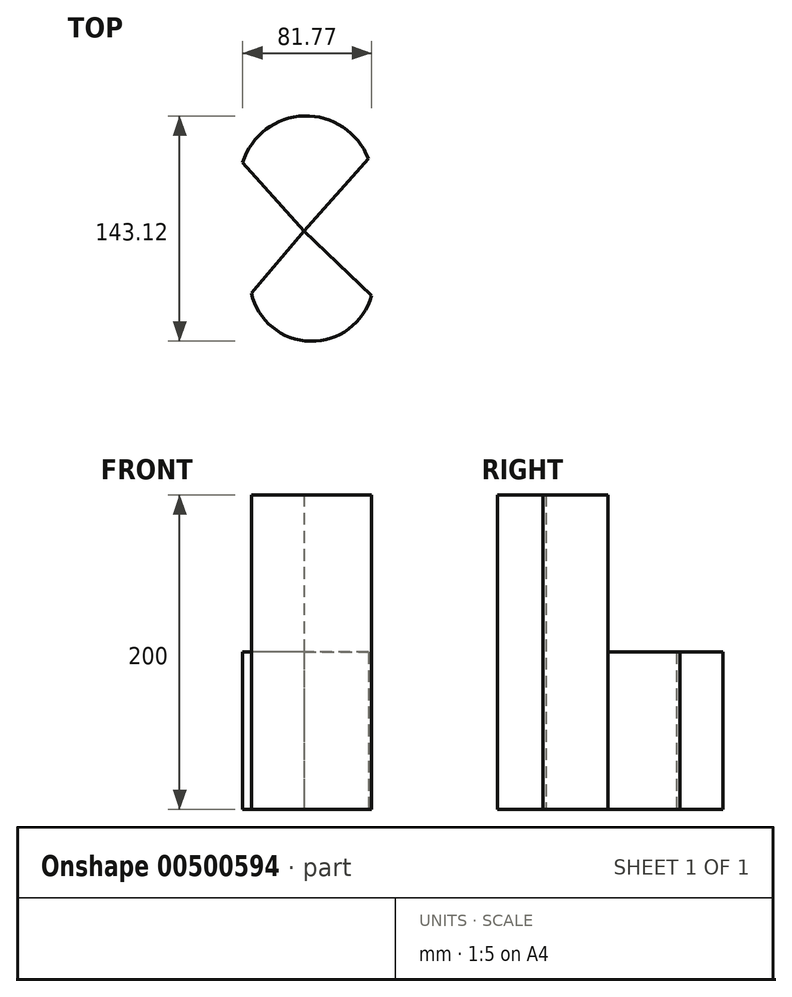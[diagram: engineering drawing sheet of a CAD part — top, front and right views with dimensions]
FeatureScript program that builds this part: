
annotation { "Feature Type Name" : "Feature", "Feature Type Description" : "" }
export const myFeature = defineFeature(function(context is Context, id is Id, definition is map)
    precondition{}
    {
        {
            var Q0;
            Q0=qCreatedBy(makeId("Top.planeOp"),FACE);
            var sketch = newSketch(context, id + "F0", { "sketchPlane" : qUnion([Q0])});
            skLineSegment(sketch, "E0", {"start": v(0, 0) * mm, "end": v(40.74, 45.76) * mm});
            skLineSegment(sketch, "E1", {"start": v(0, 0) * mm, "end": v(-39.02, 43.46) * mm});
            skLineSegment(sketch, "E2", {"start": v(0, 0) * mm, "end": v(42.75, -41.17) * mm});
            skLineSegment(sketch, "E3", {"start": v(0, 0) * mm, "end": v(-33.57, -39.45) * mm});
            skArc(sketch, "E4", {"start": v(40.74, 45.76) * mm, "mid": v(0.04, 72.96) * mm, "end": v(-39.02, 43.46) * mm});
            skArc(sketch, "E5", {"start": v(-33.57, -39.45) * mm, "mid": v(3.92, -70.13) * mm, "end": v(42.75, -41.17) * mm});
            skSolve(sketch);
        }
        {
            var Q0;
            Q0=makeQuery(id+"F0.imprint","IMPRINT",FACE,{"disambiguationData":[TD([[makeQuery(id+"F0.imprint","IMPRINT",EDGE,{"derivedFrom":sQuery(id+"F0.wireOp",EDGE,"E0")}),1.0]])]});
            var Q1;
            Q1=makeQuery(id+"F0.imprint","IMPRINT",FACE,{"disambiguationData":[TD([[makeQuery(id+"F0.imprint","IMPRINT",EDGE,{"derivedFrom":sQuery(id+"F0.wireOp",EDGE,"E2")}),-1.0]])]});
            extrude(context, id + "F1", {"entities" : qUnion([Q0, Q1]), "depth" : 100 * mm});
        }
        {
            var Q0;
            Q0=makeQuery(id+"F1.opExtrude","CAP_FACE",FACE,{"disambiguationData":[OSD([sQuery(id+"F0.wireOp",EDGE,"E2"),sQuery(id+"F0.wireOp",EDGE,"E3"),sQuery(id+"F0.wireOp",EDGE,"E5")])],"isStart":false});
            var Q1;
            Q1=makeQuery(id+"F1.opExtrude","CAP_FACE",FACE,{"disambiguationData":[OSD([sQuery(id+"F0.wireOp",EDGE,"E2"),sQuery(id+"F0.wireOp",EDGE,"E3"),sQuery(id+"F0.wireOp",EDGE,"E5")])],"isStart":true});
            extrude(context, id + "F2", {"entities" : qUnion([Q0, Q1]), "operationType" : NewBodyOperationType.ADD, "depth" : 100 * mm});
        }
    });
